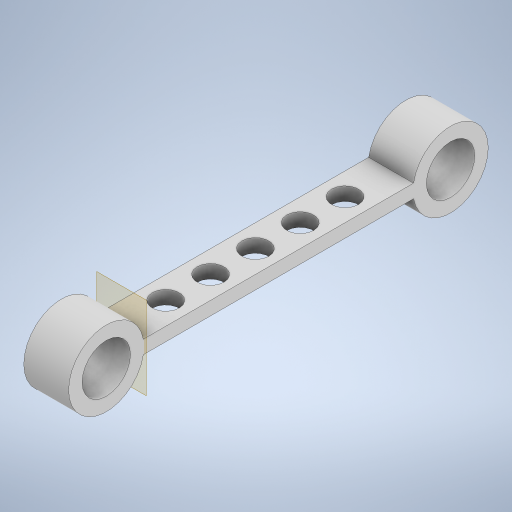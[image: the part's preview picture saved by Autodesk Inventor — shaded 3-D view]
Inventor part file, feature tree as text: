
AUTODESK INVENTOR PART (.ipt)
format: ipt  version: 2024 (Build 280153000, 153)  size: 300,544 bytes
history: native  units: mm
features: other x4, extrude x4, sketch x3, projected_geometry x2
ambient origin geometry x8: Origin, YZ Plane, XZ Plane, XY Plane, X Axis, Y Axis, Z Axis, Center Point
bodies: Body1 (feature_tree)
feature tree (13):
  other  "솔리드1"
  extrude  "돌출1"  Depth=10.8mm
  other  "작업 평면1"
  sketch  "스케치2"
  extrude  "돌출2"  Depth=16.8mm
  extrude  "돌출3"  Depth=10.0mm TaperAngle=0.0deg
  sketch  "스케치4"
  other  "작업 평면4"
  extrude  "돌출4"  Depth=38.4mm
  sketch  "스케치1"
  projected_geometry  "투영된 루프1"
  projected_geometry  "투영된 루프2"
  other  "작업 평면3"
